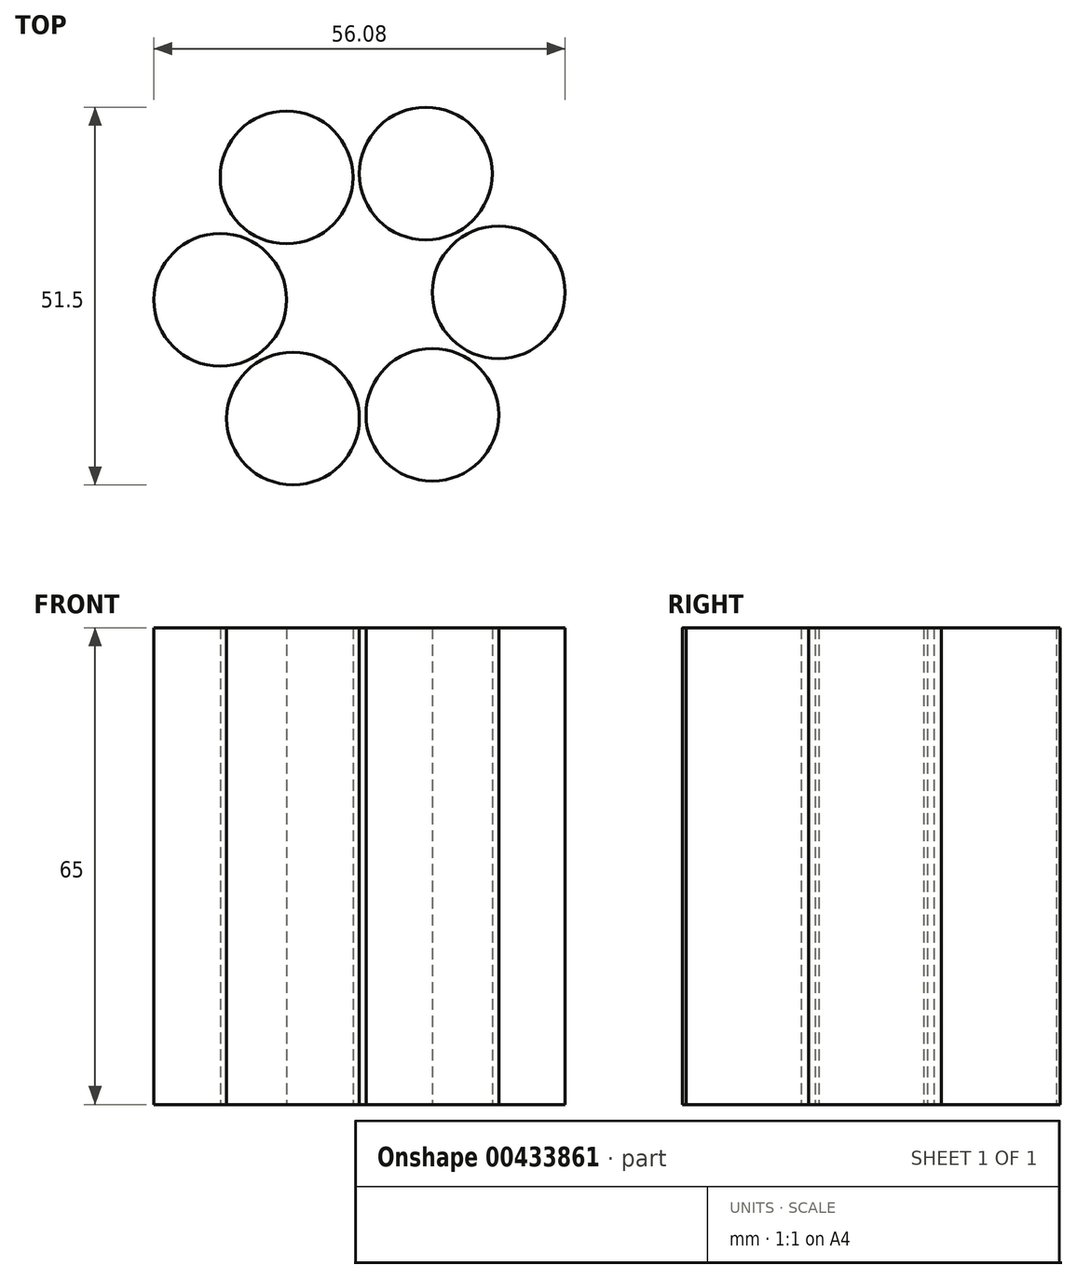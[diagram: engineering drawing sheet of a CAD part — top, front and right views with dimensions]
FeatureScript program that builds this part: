
annotation { "Feature Type Name" : "Feature", "Feature Type Description" : "" }
export const myFeature = defineFeature(function(context is Context, id is Id, definition is map)
    precondition{}
    {
        {
            var Q0;
            Q0=qCreatedBy(makeId("Top.planeOp"),FACE);
            var sketch = newSketch(context, id + "F0", { "sketchPlane" : qUnion([Q0])});
            skCircle(sketch, "E0", {"center": v(0, 0) * mm, "radius": 19 * mm});
            skCircle(sketch, "E1", {"center": v(9.05, 16.7) * mm, "radius": 9.05 * mm});
            skCircle(sketch, "E2", {"center": v(0, 0) * mm, "radius": 28.05 * mm});
            skSolve(sketch);
        }
        {
            var Q0;
            {var subQ0=sQuery(id+"F0.wireOp",EDGE,"E1");var subQ1=sQuery(id+"F0.wireOp",EDGE,"E0");var subQ2=makeQuery(id+"F0.imprint","INTERSECT",VERTEX,{"disambiguationData":[OD(0.0)],"derivedFrom":[subQ1,subQ0]});Q0=makeQuery(id+"F0.imprint","IMPRINT",FACE,{"disambiguationData":[TD([[makeQuery(id+"F0.imprint","IMPRINT",EDGE,{"disambiguationData":[TD([[subQ2,1.0]])],"derivedFrom":subQ1}),-1.0]])]});}
            var Q1;
            {var subQ0=sQuery(id+"F0.wireOp",EDGE,"E1");var subQ1=sQuery(id+"F0.wireOp",EDGE,"E0");var subQ2=makeQuery(id+"F0.imprint","INTERSECT",VERTEX,{"disambiguationData":[OD(0.0)],"derivedFrom":[subQ1,subQ0]});Q1=makeQuery(id+"F0.imprint","IMPRINT",FACE,{"disambiguationData":[TD([[makeQuery(id+"F0.imprint","IMPRINT",EDGE,{"disambiguationData":[TD([[subQ2,1.0]])],"derivedFrom":subQ1}),1.0]])]});}
            var Q2;
            Q2=makeQuery(id+"F0.imprint","IMPRINT",FACE,{"disambiguationData":[TD([[makeQuery(id+"F0.imprint","IMPRINT",EDGE,{"derivedFrom":sQuery(id+"F0.wireOp",EDGE,"tUcA8ytC-8aOl-5LnD-rwcT-RsDwppVZC7tc")}),1.0]])]});
            extrude(context, id + "F1", {"entities" : qUnion([Q0, Q1, Q2]), "depth" : 65 * mm});
        }
        {
            var Q0;
            Q0=makeQuery(id+"F1.opExtrude","SWEPT_BODY",BODY,{"disambiguationData":[OSD([sQuery(id+"F0.wireOp",EDGE,"E1")])]});
            var Q1;
            Q1=sQuery(id+"F0.wireOp",EDGE,"E0");
            circularPattern(context, id + "F2", {"entities" : qUnion([Q0]), "axis" : qUnion([Q1]), "angle" : 360 * degree, "instanceCount" : 6, "equalSpace" : true, "computeTransformsWithoutBuiltin" : true});
        }
        {
            var Q0;
            Q0=qCreatedBy(makeId("Front.planeOp"),FACE);
            cPlane(context, id + "F3", {"entities" : qUnion([Q0]), "cplaneType" : CPlaneType.OFFSET, "offset" : 26 * mm, "width" : 150 * mm, "height" : 150 * mm});
        }
    });
